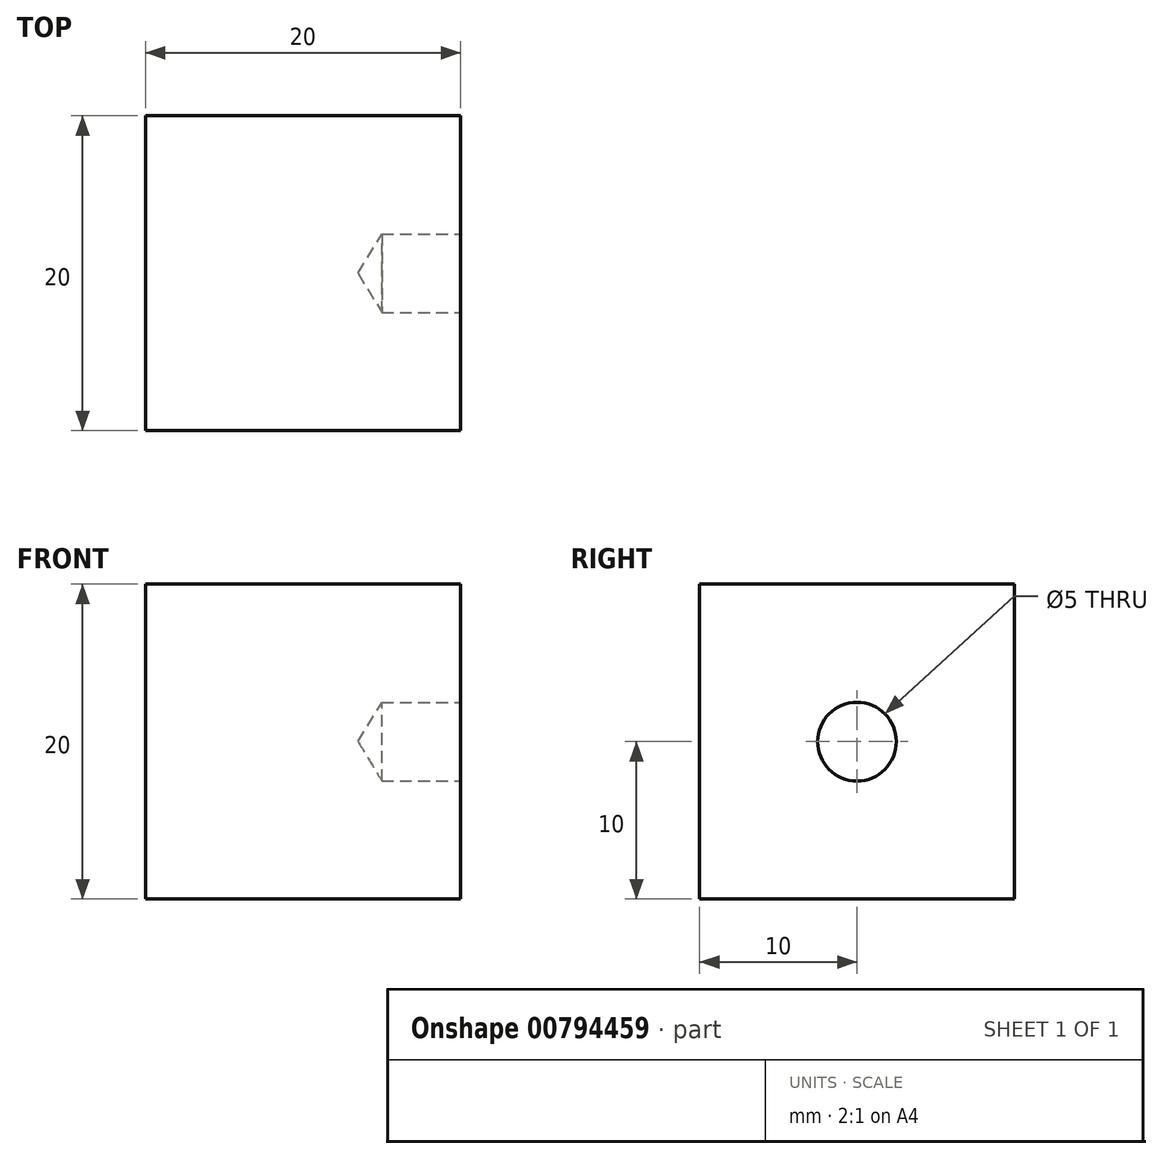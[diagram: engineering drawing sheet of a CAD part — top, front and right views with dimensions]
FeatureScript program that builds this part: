
annotation { "Feature Type Name" : "Feature", "Feature Type Description" : "" }
export const myFeature = defineFeature(function(context is Context, id is Id, definition is map)
    precondition{}
    {
        {
            var Q0;
            Q0=qCreatedBy(makeId("Top.planeOp"),FACE);
            var sketch = newSketch(context, id + "F0", { "sketchPlane" : qUnion([Q0])});
            skLineSegment(sketch, "E0.bottom", {"start": v(-51.57, 20) * mm, "end": v(-31.57, 20) * mm});
            skLineSegment(sketch, "E0.top", {"start": v(-51.57, 0) * mm, "end": v(-31.57, 0) * mm});
            skLineSegment(sketch, "E0.left", {"start": v(-51.57, 20) * mm, "end": v(-51.57, 0) * mm});
            skLineSegment(sketch, "E0.right", {"start": v(-31.57, 20) * mm, "end": v(-31.57, 0) * mm});
            skSolve(sketch);
        }
        {
            var Q0;
            Q0=makeQuery(id+"F0.imprint","IMPRINT",FACE,{"disambiguationData":[TD([[makeQuery(id+"F0.imprint","IMPRINT",EDGE,{"derivedFrom":sQuery(id+"F0.wireOp",EDGE,"E0.bottom")}),-1.0]])]});
            extrude(context, id + "F1", {"entities" : qUnion([Q0]), "depth" : 20 * mm, "offsetDistance" : 25 * mm});
        }
        {
            var Q0;
            Q0=makeQuery(id+"F1.opExtrude","SWEPT_FACE",FACE,{"disambiguationData":[OSD([sQuery(id+"F0.wireOp",EDGE,"E0.right")])]});
            var sketch = newSketch(context, id + "F2", { "sketchPlane" : qUnion([Q0])});
            skLineSegment(sketch, "E1", {"start": v(0, 10) * mm, "end": v(20, 10) * mm});
            skPoint(sketch, "E2", {"position": v(10, 10) * mm});
            skSolve(sketch);
        }
        {
            var Q0;
            Q0=sQuery(id+"F2.wireOp",VERTEX,"E2");
            var Q1;
            Q1=makeQuery(id+"F1.opExtrude","SWEPT_BODY",BODY,{"disambiguationData":[OSD([sQuery(id+"F0.wireOp",EDGE,"E0.bottom"),sQuery(id+"F0.wireOp",EDGE,"E0.top"),sQuery(id+"F0.wireOp",EDGE,"E0.left"),sQuery(id+"F0.wireOp",EDGE,"E0.right")])]});
            hole(context, id + "F3", {"style" : HoleStyle.SIMPLE, "endStyle" : HoleEndStyle.BLIND, "holeDiameter" : 5 * mm, "majorDiameter" : 5 * mm, "holeDepth" : 5 * mm, "isTappedThrough" : true, "tappedDepth" : 12 * mm, "tapClearance" : 3, "locations" : qUnion([Q0]), "scope" : qUnion([Q1])});
        }
    });
